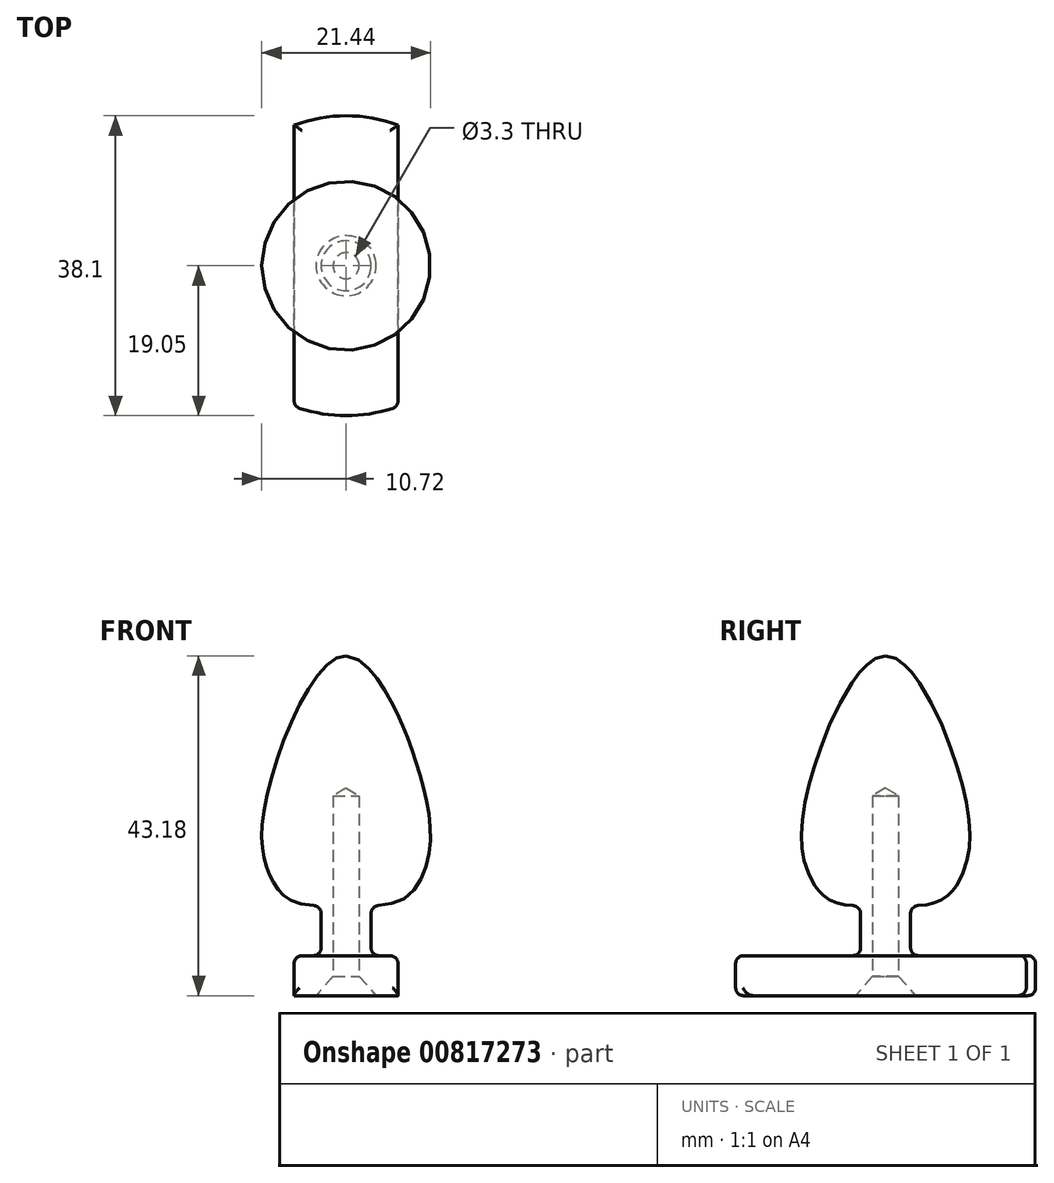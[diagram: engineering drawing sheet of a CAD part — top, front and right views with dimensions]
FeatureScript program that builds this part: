
annotation { "Feature Type Name" : "Feature", "Feature Type Description" : "" }
export const myFeature = defineFeature(function(context is Context, id is Id, definition is map)
    precondition{}
    {
        {
            var Q0;
            Q0=qCreatedBy(makeId("Front.planeOp"),FACE);
            var sketch = newSketch(context, id + "F0", { "sketchPlane" : qUnion([Q0])});
            skLineSegment(sketch, "E0", {"start": v(-3.18, 0) * mm, "end": v(-3.18, 6.35) * mm});
            skLineSegment(sketch, "E1", {"start": v(-3.18, 0) * mm, "end": v(-19.05, 0) * mm});
            skLineSegment(sketch, "E2", {"start": v(-19.05, 0) * mm, "end": v(-19.05, -5.08) * mm});
            skLineSegment(sketch, "E3", {"start": v(-19.05, -5.08) * mm, "end": v(0, -5.08) * mm});
            skFitSpline(sketch, "E4", {"points": [v(-3.18, 6.35) * mm, v(-9.53, 9.85) * mm, v(-10.21, 19.66) * mm, v(0, 38.1) * mm], "startDerivative": vector(-46.96, -0.68) * mm, "endDerivative": vector(27.73, 0) * mm});
            skFitSpline(sketch, "E5.MirrorCS", {"points": [v(3.18, 6.35) * mm, v(9.53, 9.85) * mm, v(10.21, 19.66) * mm, v(0, 38.1) * mm], "startDerivative": vector(46.96, -0.68) * mm, "endDerivative": vector(-27.73, 0) * mm});
            skLineSegment(sketch, "E6.MirrorCS", {"start": v(3.18, 0) * mm, "end": v(3.18, 6.35) * mm});
            skLineSegment(sketch, "E7.MirrorCS", {"start": v(3.18, 0) * mm, "end": v(19.05, 0) * mm});
            skLineSegment(sketch, "E8.MirrorCS", {"start": v(19.05, 0) * mm, "end": v(19.05, -5.08) * mm});
            skLineSegment(sketch, "E9.MirrorCS", {"start": v(19.05, -5.08) * mm, "end": v(0, -5.08) * mm});
            skLineSegment(sketch, "E10", {"start": v(0, 52.02) * mm, "end": v(0, -27.64) * mm});
            skSolve(sketch);
        }
        {
            var Q0;
            Q0=makeQuery(id+"F0.imprint","IMPRINT",FACE,{"disambiguationData":[TD([[makeQuery(id+"F0.imprint","IMPRINT",EDGE,{"derivedFrom":sQuery(id+"F0.wireOp",EDGE,"E0")}),-1.0]])]});
            var Q1;
            Q1=sQuery(id+"F0.wireOp",EDGE,"E10");
            revolve(context, id + "F1", {"surfaceOperationType" : NewSurfaceOperationType.NEW, "entities" : qUnion([Q0]), "axis" : qUnion([Q1]), "revolveType" : RevolveType.FULL});
        }
        {
            var Q0;
            Q0=makeQuery(id+"F1.opRevolve","SWEPT_FACE",FACE,{"disambiguationData":[OSD([sQuery(id+"F0.wireOp",EDGE,"E3")])]});
            var sketch = newSketch(context, id + "F2", { "sketchPlane" : qUnion([Q0])});
            skPoint(sketch, "E11", {"position": v(0, 0) * mm});
            skSolve(sketch);
        }
        {
            var Q0;
            Q0=sQuery(id+"F2.wireOp",VERTEX,"E11");
            var Q1;
            Q1=makeQuery(id+"F1.opRevolve","SWEPT_BODY",BODY,{"disambiguationData":[OSD([sQuery(id+"F0.wireOp",EDGE,"E0"),sQuery(id+"F0.wireOp",EDGE,"E1"),sQuery(id+"F0.wireOp",EDGE,"E2"),sQuery(id+"F0.wireOp",EDGE,"E3"),sQuery(id+"F0.wireOp",EDGE,"E4"),sQuery(id+"F0.wireOp",EDGE,"E10")])]});
            hole(context, id + "F3", {"style" : HoleStyle.C_SINK, "endStyle" : HoleEndStyle.BLIND, "holeDiameter" : 3.3 * mm, "cSinkDiameter" : 7.62 * mm, "cSinkAngle" : 82 * degree, "majorDiameter" : 6.35 * mm, "holeDepth" : 25.4 * mm, "isTappedThrough" : true, "tappedDepth" : 12.7 * mm, "tapClearance" : 3, "locations" : qUnion([Q0]), "scope" : qUnion([Q1])});
        }
        {
            var Q0;
            Q0=makeQuery(id+"F1.opRevolve","SWEPT_FACE",FACE,{"disambiguationData":[OSD([sQuery(id+"F0.wireOp",EDGE,"E3")])]});
            var sketch = newSketch(context, id + "F4", { "sketchPlane" : qUnion([Q0])});
            skLineSegment(sketch, "E12", {"start": v(-6.6, 17.87) * mm, "end": v(-6.6, -17.87) * mm});
            skArc(sketch, "E13", {"start": v(-6.6, 17.87) * mm, "mid": v(-19.05, 0) * mm, "end": v(-6.6, -17.87) * mm});
            skLineSegment(sketch, "E14.MirrorCS", {"start": v(6.6, 17.87) * mm, "end": v(6.6, -17.87) * mm});
            skArc(sketch, "E15.MirrorCS", {"start": v(6.6, 17.87) * mm, "mid": v(19.05, 0) * mm, "end": v(6.6, -17.87) * mm});
            skSolve(sketch);
        }
        {
            var Q0;
            Q0=makeQuery(id+"F4.imprint","IMPRINT",FACE,{"disambiguationData":[TD([[makeQuery(id+"F4.imprint","IMPRINT",EDGE,{"derivedFrom":sQuery(id+"F4.wireOp",EDGE,"E12")}),-1.0]])]});
            var Q1;
            Q1=makeQuery(id+"F4.imprint","IMPRINT",FACE,{"disambiguationData":[TD([[makeQuery(id+"F4.imprint","IMPRINT",EDGE,{"derivedFrom":sQuery(id+"F4.wireOp",EDGE,"E14.MirrorCS")}),1.0]])]});
            extrude(context, id + "F5", {"entities" : qUnion([Q0, Q1]), "operationType" : NewBodyOperationType.REMOVE, "oppositeDirection" : true, "depth" : 7.62 * mm, "offsetDistance" : 25.4 * mm});
        }
        {
            var Q0;
            Q0=makeQuery(id+"F1.opRevolve","SWEPT_EDGE",EDGE,{"disambiguationData":[OSD([sQuery(id+"F0.wireOp",EDGE,"E0"),sQuery(id+"F0.wireOp",EDGE,"E4")])]});
            var Q1;
            Q1=makeQuery(id+"F1.opRevolve","SWEPT_EDGE",EDGE,{"disambiguationData":[OSD([sQuery(id+"F0.wireOp",EDGE,"E0"),sQuery(id+"F0.wireOp",EDGE,"E1")])]});
            var Q2;
            Q2=makeQuery(id+"F1.opRevolve","SWEPT_EDGE",EDGE,{"disambiguationData":[OSD([sQuery(id+"F0.wireOp",EDGE,"E1"),sQuery(id+"F0.wireOp",EDGE,"E2")])]});
            var Q3;
            Q3=makeQuery(id+"F1.opRevolve","SWEPT_EDGE",EDGE,{"disambiguationData":[OSD([sQuery(id+"F0.wireOp",EDGE,"E2"),sQuery(id+"F0.wireOp",EDGE,"E3")])]});
            var Q4;
            Q4=makeQuery(id+"F5.boolean.opBoolean","COPY",EDGE,{"derivedFrom":makeQuery(id+"F5.opExtrude","CAP_EDGE",EDGE,{"disambiguationData":[OSD([sQuery(id+"F4.wireOp",EDGE,"E12")])],"isStart":true})});
            var Q5;
            Q5=makeQuery(id+"F5.boolean.opBoolean","COPY",EDGE,{"derivedFrom":makeQuery(id+"F5.opExtrude","CAP_EDGE",EDGE,{"disambiguationData":[OSD([sQuery(id+"F4.wireOp",EDGE,"E14.MirrorCS")])],"isStart":true})});
            var Q6;
            Q6=makeQuery(id+"F5.boolean.opBoolean","INTERSECT",EDGE,{"derivedFrom":[makeQuery(id+"F1.opRevolve","SWEPT_FACE",FACE,{"disambiguationData":[OSD([sQuery(id+"F0.wireOp",EDGE,"E1")])]}),makeQuery(id+"F5.opExtrude","SWEPT_FACE",FACE,{"disambiguationData":[OSD([sQuery(id+"F4.wireOp",EDGE,"E12")])]})]});
            var Q7;
            Q7=makeQuery(id+"F5.boolean.opBoolean","INTERSECT",EDGE,{"derivedFrom":[makeQuery(id+"F1.opRevolve","SWEPT_FACE",FACE,{"disambiguationData":[OSD([sQuery(id+"F0.wireOp",EDGE,"E1")])]}),makeQuery(id+"F5.opExtrude","SWEPT_FACE",FACE,{"disambiguationData":[OSD([sQuery(id+"F4.wireOp",EDGE,"E14.MirrorCS")])]})]});
            var Q8;
            {var subQ0=sQuery(id+"F4.wireOp",EDGE,"E15.MirrorCS");var subQ1=sQuery(id+"F4.wireOp",EDGE,"E14.MirrorCS");var subQ2=sQuery(id+"F0.wireOp",EDGE,"E3");var subQ3=sQuery(id+"F0.wireOp",EDGE,"E2");Q8=makeQuery(id+"F5.boolean.opBoolean","COPY",EDGE,{"derivedFrom":makeQuery(id+"F5.opExtrude","SWEPT_EDGE",EDGE,{"disambiguationData":[OSD([subQ3,subQ2,subQ1,subQ0]),TDD([makeQuery(id+"F4.imprint","INTERSECT",VERTEX,{"disambiguationData":[OD(0.0)],"derivedFrom":[makeQuery(id+"F1.opRevolve","SWEPT_EDGE",EDGE,{"disambiguationData":[OSD([subQ3,subQ2])]}),subQ1,subQ0]})])]})});}
            var Q9;
            {var subQ0=sQuery(id+"F4.wireOp",EDGE,"E15.MirrorCS");var subQ1=sQuery(id+"F4.wireOp",EDGE,"E14.MirrorCS");var subQ2=sQuery(id+"F0.wireOp",EDGE,"E3");var subQ3=sQuery(id+"F0.wireOp",EDGE,"E2");Q9=makeQuery(id+"F5.boolean.opBoolean","COPY",EDGE,{"derivedFrom":makeQuery(id+"F5.opExtrude","SWEPT_EDGE",EDGE,{"disambiguationData":[OSD([subQ3,subQ2,subQ1,subQ0]),TDD([makeQuery(id+"F4.imprint","INTERSECT",VERTEX,{"disambiguationData":[OD(1.0)],"derivedFrom":[makeQuery(id+"F1.opRevolve","SWEPT_EDGE",EDGE,{"disambiguationData":[OSD([subQ3,subQ2])]}),subQ1,subQ0]})])]})});}
            var Q10;
            {var subQ0=sQuery(id+"F4.wireOp",EDGE,"E13");var subQ1=sQuery(id+"F4.wireOp",EDGE,"E12");var subQ2=sQuery(id+"F0.wireOp",EDGE,"E3");var subQ3=sQuery(id+"F0.wireOp",EDGE,"E2");Q10=makeQuery(id+"F5.boolean.opBoolean","COPY",EDGE,{"derivedFrom":makeQuery(id+"F5.opExtrude","SWEPT_EDGE",EDGE,{"disambiguationData":[OSD([subQ3,subQ2,subQ1,subQ0]),TDD([makeQuery(id+"F4.imprint","INTERSECT",VERTEX,{"disambiguationData":[OD(0.0)],"derivedFrom":[makeQuery(id+"F1.opRevolve","SWEPT_EDGE",EDGE,{"disambiguationData":[OSD([subQ3,subQ2])]}),subQ1,subQ0]})])]})});}
            var Q11;
            {var subQ0=sQuery(id+"F4.wireOp",EDGE,"E13");var subQ1=sQuery(id+"F4.wireOp",EDGE,"E12");var subQ2=sQuery(id+"F0.wireOp",EDGE,"E3");var subQ3=sQuery(id+"F0.wireOp",EDGE,"E2");Q11=makeQuery(id+"F5.boolean.opBoolean","COPY",EDGE,{"derivedFrom":makeQuery(id+"F5.opExtrude","SWEPT_EDGE",EDGE,{"disambiguationData":[OSD([subQ3,subQ2,subQ1,subQ0]),TDD([makeQuery(id+"F4.imprint","INTERSECT",VERTEX,{"disambiguationData":[OD(1.0)],"derivedFrom":[makeQuery(id+"F1.opRevolve","SWEPT_EDGE",EDGE,{"disambiguationData":[OSD([subQ3,subQ2])]}),subQ1,subQ0]})])]})});}
            fillet(context, id + "F6", {"entities" : qUnion([Q0, Q1, Q2, Q3, Q4, Q5, Q6, Q7, Q8, Q9, Q10, Q11]), "radius" : 1.02 * mm, "tangentPropagation" : true, "allowEdgeOverflow" : false});
        }
    });
